annotation { "Feature Type Name" : "Feature", "Feature Type Description" : "" }
export const myFeature = defineFeature(function(context is Context, id is Id, definition is map)
    precondition{}
    {
        {
            var Q0;
            Q0=qCreatedBy(makeId("Top.planeOp"),FACE);
            var sketch = newSketch(context, id + "F0", { "sketchPlane" : qUnion([Q0])});
            skCircle(sketch, "E0", {"center": v(0, 0) * mm, "radius": 25 * mm});
            skSolve(sketch);
        }
        {
            var Q0;
            Q0 = qSketchRegion(id + "F0", true);
            var Q1;
            Q1=makeQuery(id+"F0.imprint","IMPRINT",FACE,{"disambiguationData":[TD([[makeQuery(id+"F0.imprint","IMPRINT",EDGE,{"derivedFrom":sQuery(id+"F0.wireOp",EDGE,"E0")}),1.0]])]});
            extrude(context, id + "F1", {"entities" : qUnion([Q0, Q1]), "depth" : 1 * mm});
        }
        {
            var Q0;
            Q0=makeQuery(id+"F1.opExtrude","CAP_FACE",FACE,{"disambiguationData":[OSD([sQuery(id+"F0.wireOp",EDGE,"E0")])],"isStart":false});
            var sketch = newSketch(context, id + "F2", { "sketchPlane" : qUnion([Q0])});
            skCircle(sketch, "E1", {"center": v(0, 0) * mm, "radius": 22.5 * mm});
            skSolve(sketch);
        }
        {
            var Q0;
            Q0=makeQuery(id+"F2.imprint","IMPRINT",FACE,{"disambiguationData":[TD([[makeQuery(id+"F2.imprint","IMPRINT",EDGE,{"derivedFrom":sQuery(id+"F2.wireOp",EDGE,"E1")}),-1.0]])]});
            extrude(context, id + "F3", {"entities" : qUnion([Q0]), "operationType" : NewBodyOperationType.ADD, "depth" : 1 * mm});
        }
        {
            var Q0;
            Q0=makeQuery(id+"F1.opExtrude","CAP_FACE",FACE,{"disambiguationData":[OSD([sQuery(id+"F0.wireOp",EDGE,"E0")])],"isStart":false});
            var sketch = newSketch(context, id + "F4", { "sketchPlane" : qUnion([Q0])});
            skText(sketch, "E2", { "text": "SPELLING BEE", "fontName": "OpenSans-Bold.ttf"});
            skText(sketch, "E3", { "text": "ONE OF THE BEST", "fontName": "OpenSans-Bold.ttf"});
            skCircle(sketch, "E4.cCircle", {"center": v(0, -1.98) * mm, "radius": 5.05 * mm, "construction": true});
            skLineSegment(sketch, "E4.0", {"start": v(-5.07, 0.91) * mm, "end": v(-0.03, 3.86) * mm});
            skLineSegment(sketch, "E4.1", {"start": v(-0.03, 3.86) * mm, "end": v(5.04, 0.96) * mm});
            skLineSegment(sketch, "E4.2", {"start": v(5.04, 0.96) * mm, "end": v(5.07, -4.87) * mm});
            skLineSegment(sketch, "E4.3", {"start": v(5.07, -4.87) * mm, "end": v(0.03, -7.81) * mm});
            skLineSegment(sketch, "E4.4", {"start": v(0.03, -7.81) * mm, "end": v(-5.04, -4.92) * mm});
            skLineSegment(sketch, "E4.5", {"start": v(-5.04, -4.92) * mm, "end": v(-5.07, 0.91) * mm});
            skPoint(sketch, "E4.0.midPoint", {"position": v(-2.55, 2.38) * mm});
            const initialGuessF4  = {"E2": [-0.02046, 0.00502, 1, 0, 0.00434], "E3": [-0.01906, -0.01195, 1, 0, 0.0032]};
            skSetInitialGuess(sketch, initialGuessF4);
            skSolve(sketch);
        }
        {
            var Q0;
            Q0 = qSketchRegion(id + "F4", true);
            extrude(context, id + "F5", {"entities" : qUnion([Q0]), "operationType" : NewBodyOperationType.ADD, "depth" : 0.5 * mm});
        }
    });